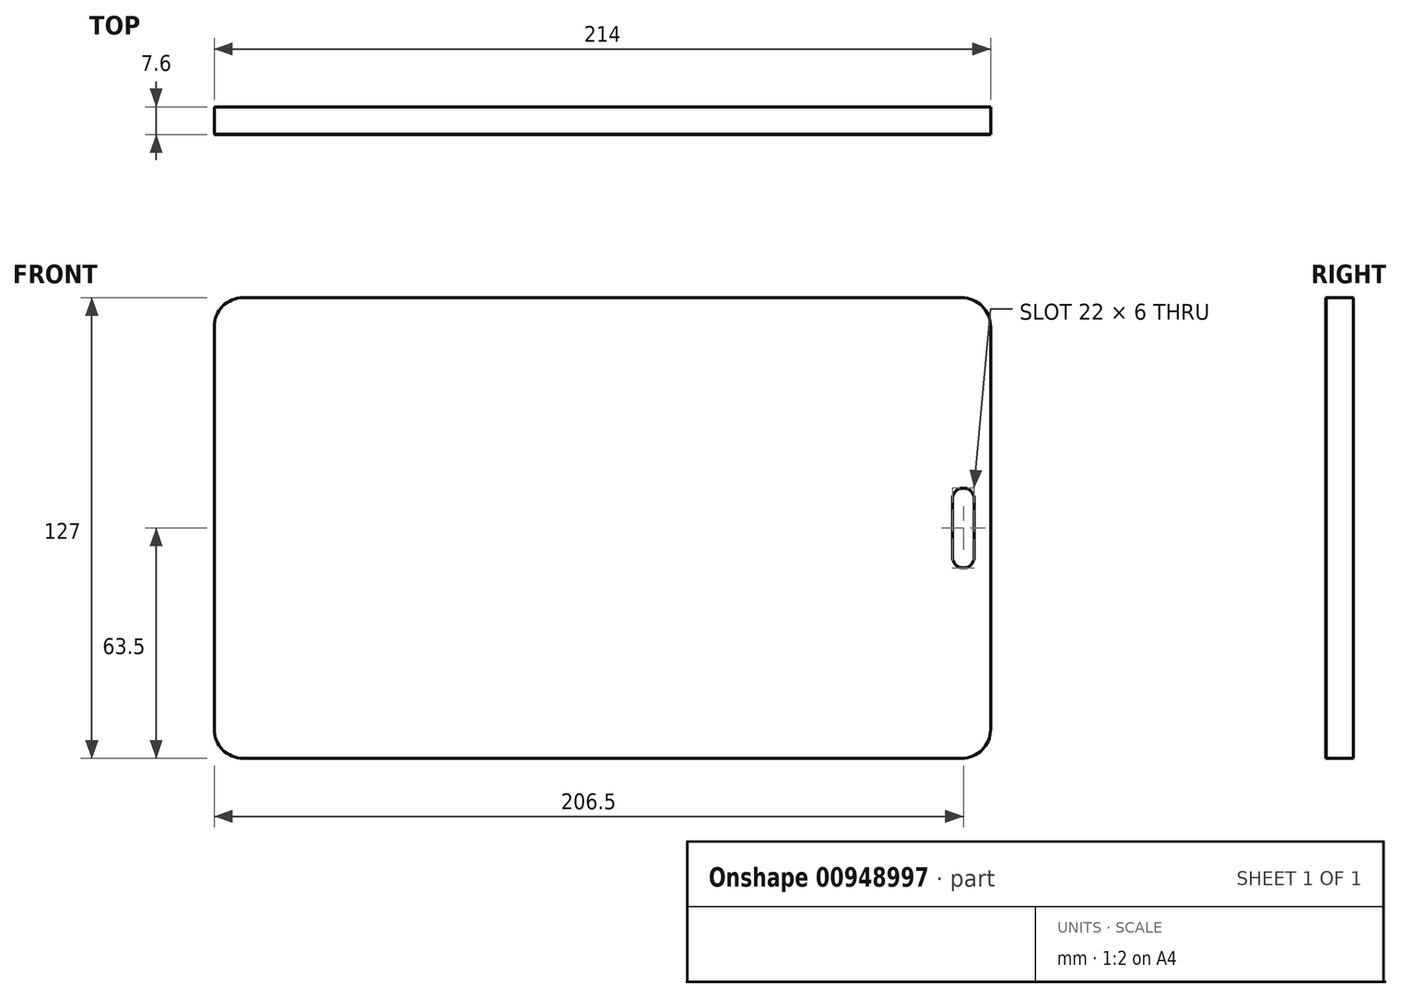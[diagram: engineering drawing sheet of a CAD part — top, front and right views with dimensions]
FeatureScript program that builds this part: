
annotation { "Feature Type Name" : "Feature", "Feature Type Description" : "" }
export const myFeature = defineFeature(function(context is Context, id is Id, definition is map)
    precondition{}
    {
        {
            var Q0;
            Q0=qCreatedBy(makeId("Front.planeOp"),FACE);
            var sketch = newSketch(context, id + "F0", { "sketchPlane" : qUnion([Q0])});
            skLineSegment(sketch, "E0.bottom", {"start": v(107, -63.5) * mm, "end": v(-107, -63.5) * mm});
            skLineSegment(sketch, "E0.top", {"start": v(107, 63.5) * mm, "end": v(-107, 63.5) * mm});
            skLineSegment(sketch, "E0.left", {"start": v(107, -63.5) * mm, "end": v(107, 63.5) * mm});
            skLineSegment(sketch, "E0.right", {"start": v(-107, -63.5) * mm, "end": v(-107, 63.5) * mm});
            skPoint(sketch, "E0.middle", {"position": v(0, 0) * mm});
            skSolve(sketch);
        }
        {
            var Q0;
            Q0 = qSketchRegion(id + "F0", true);
            extrude(context, id + "F1", {"entities" : qUnion([Q0]), "endBound" : BoundingType.SYMMETRIC, "depth" : 7.5 * mm, "offsetDistance" : 25 * mm});
        }
        {
            var Q0;
            Q0=makeQuery(id+"F1.opExtrude","SWEPT_EDGE",EDGE,{"disambiguationData":[OSD([sQuery(id+"F0.wireOp",EDGE,"E0.top"),sQuery(id+"F0.wireOp",EDGE,"E0.left")])]});
            var Q1;
            Q1=makeQuery(id+"F1.opExtrude","SWEPT_EDGE",EDGE,{"disambiguationData":[OSD([sQuery(id+"F0.wireOp",EDGE,"E0.bottom"),sQuery(id+"F0.wireOp",EDGE,"E0.left")])]});
            var Q2;
            Q2=makeQuery(id+"F1.opExtrude","SWEPT_EDGE",EDGE,{"disambiguationData":[OSD([sQuery(id+"F0.wireOp",EDGE,"E0.top"),sQuery(id+"F0.wireOp",EDGE,"E0.right")])]});
            var Q3;
            Q3=makeQuery(id+"F1.opExtrude","SWEPT_EDGE",EDGE,{"disambiguationData":[OSD([sQuery(id+"F0.wireOp",EDGE,"E0.bottom"),sQuery(id+"F0.wireOp",EDGE,"E0.right")])]});
            fillet(context, id + "F2", {"entities" : qUnion([Q0, Q1, Q2, Q3]), "radius" : 8 * mm, "tangentPropagation" : true, "allowEdgeOverflow" : false});
        }
        {
            var Q0;
            Q0=makeQuery(id+"F1.opExtrude","CAP_FACE",FACE,{"disambiguationData":[OSD([sQuery(id+"F0.wireOp",EDGE,"E0.bottom"),sQuery(id+"F0.wireOp",EDGE,"E0.top"),sQuery(id+"F0.wireOp",EDGE,"E0.left"),sQuery(id+"F0.wireOp",EDGE,"E0.right")])],"isStart":false});
            var sketch = newSketch(context, id + "F3", { "sketchPlane" : qUnion([Q0])});
            skLineSegment(sketch, "E1.0.0", {"start": v(107, -55.5) * mm, "end": v(107, 55.5) * mm});
            skArc(sketch, "E1.0.1", {"start": v(107, 55.5) * mm, "mid": v(104.66, 61.16) * mm, "end": v(99, 63.5) * mm});
            skLineSegment(sketch, "E1.0.2", {"start": v(99, 63.5) * mm, "end": v(-99, 63.5) * mm});
            skArc(sketch, "E1.0.3", {"start": v(-99, 63.5) * mm, "mid": v(-104.66, 61.16) * mm, "end": v(-107, 55.5) * mm});
            skLineSegment(sketch, "E1.0.4", {"start": v(-107, 55.5) * mm, "end": v(-107, -55.5) * mm});
            skArc(sketch, "E1.0.5", {"start": v(-107, -55.5) * mm, "mid": v(-104.66, -61.16) * mm, "end": v(-99, -63.5) * mm});
            skLineSegment(sketch, "E1.0.6", {"start": v(-99, -63.5) * mm, "end": v(99, -63.5) * mm});
            skArc(sketch, "E1.0.7", {"start": v(99, -63.5) * mm, "mid": v(104.66, -61.16) * mm, "end": v(107, -55.5) * mm});
            skLineSegment(sketch, "E2.bottom", {"start": v(-92, 58.5) * mm, "end": v(92, 58.5) * mm});
            skLineSegment(sketch, "E2.top", {"start": v(-92, -58.5) * mm, "end": v(92, -58.5) * mm});
            skLineSegment(sketch, "E2.left", {"start": v(-92, 58.5) * mm, "end": v(-92, -58.5) * mm});
            skLineSegment(sketch, "E2.right", {"start": v(92, 58.5) * mm, "end": v(92, -58.5) * mm});
            skPoint(sketch, "E2.middle", {"position": v(0, 0) * mm});
            skLineSegment(sketch, "E3", {"start": v(92, 0) * mm, "end": v(107, 0) * mm, "construction": true});
            skPoint(sketch, "E4", {"position": v(99.5, 0) * mm});
            skLineSegment(sketch, "E5", {"start": v(99.5, -8) * mm, "end": v(99.5, 8) * mm, "construction": true});
            skArc(sketch, "E6.0.startCap", {"start": v(102.5, -8) * mm, "mid": v(99.5, -11) * mm, "end": v(96.5, -8) * mm});
            skArc(sketch, "E6.0.endCap", {"start": v(96.5, 8) * mm, "mid": v(99.5, 11) * mm, "end": v(102.5, 8) * mm});
            skLineSegment(sketch, "E6.0.left", {"start": v(96.5, -8) * mm, "end": v(96.5, 8) * mm});
            skLineSegment(sketch, "E6.0.right", {"start": v(102.5, -8) * mm, "end": v(102.5, 8) * mm});
            skCircle(sketch, "E7", {"center": v(-101, 46.5) * mm, "radius": 1.5 * mm});
            skCircle(sketch, "E8", {"center": v(-102, 14.5) * mm, "radius": 1.3 * mm});
            skSolve(sketch);
        }
        {
            var Q0;
            Q0=makeQuery(id+"F3.imprint","IMPRINT",FACE,{"disambiguationData":[TD([[makeQuery(id+"F3.imprint","IMPRINT",EDGE,{"derivedFrom":sQuery(id+"F3.wireOp",EDGE,"E6.0.startCap")}),-1.0]])]});
            var Q1;
            Q1=makeQuery(id+"F3.imprint","IMPRINT",FACE,{"disambiguationData":[TD([[makeQuery(id+"F3.imprint","IMPRINT",EDGE,{"derivedFrom":sQuery(id+"F3.wireOp",EDGE,"E2.bottom")}),-1.0]])]});
            var Q2;
            Q2=makeQuery(id+"F3.imprint","IMPRINT",FACE,{"disambiguationData":[TD([[makeQuery(id+"F3.imprint","IMPRINT",EDGE,{"derivedFrom":sQuery(id+"F3.wireOp",EDGE,"E8")}),1.0]])]});
            var Q3;
            Q3=makeQuery(id+"F3.imprint","IMPRINT",FACE,{"disambiguationData":[TD([[makeQuery(id+"F3.imprint","IMPRINT",EDGE,{"derivedFrom":sQuery(id+"F3.wireOp",EDGE,"E7")}),1.0]])]});
            extrude(context, id + "F4", {"entities" : qUnion([Q0, Q1, Q2, Q3]), "depth" : .1 * mm, "offsetDistance" : 25 * mm});
        }
    });
